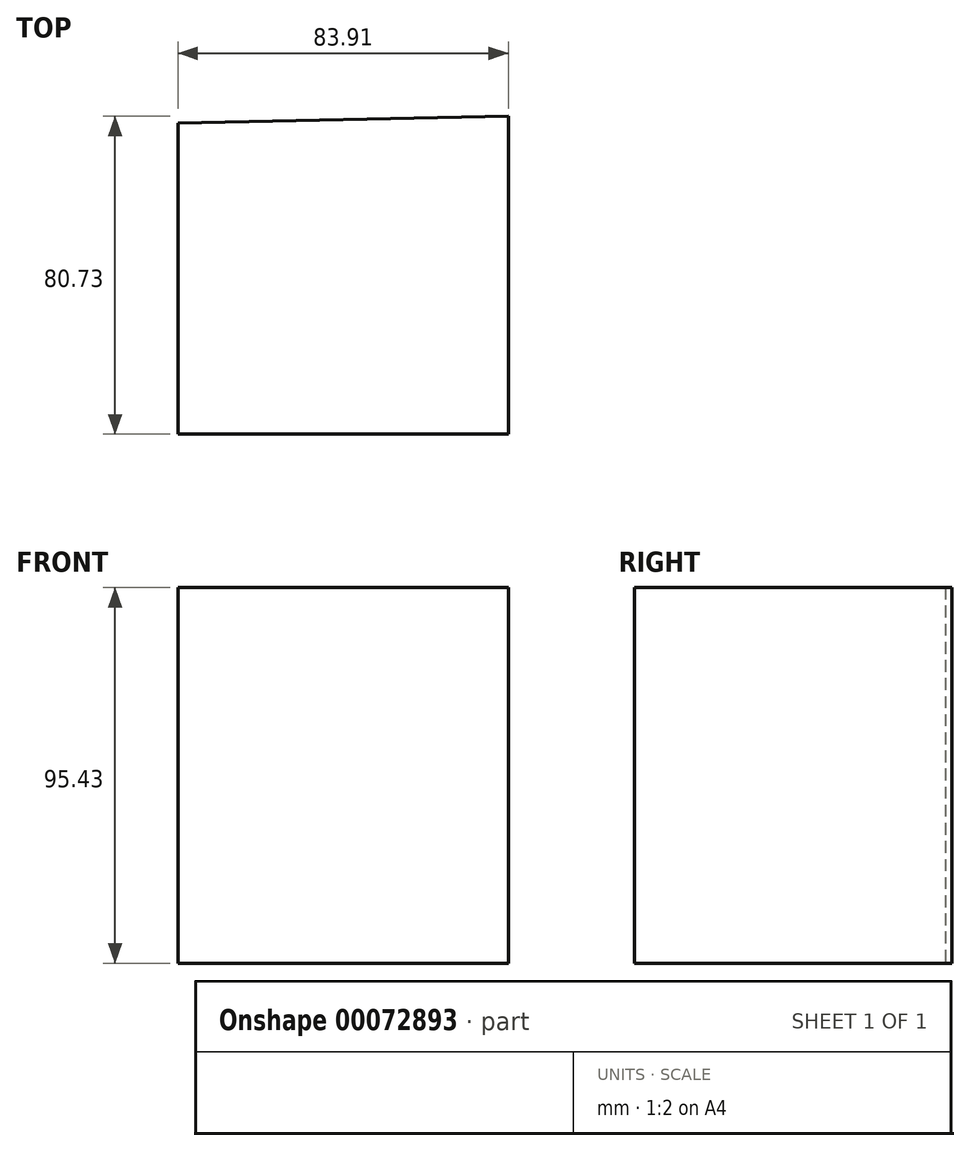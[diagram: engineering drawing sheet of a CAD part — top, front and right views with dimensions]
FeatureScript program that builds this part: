
annotation { "Feature Type Name" : "Feature", "Feature Type Description" : "" }
export const myFeature = defineFeature(function(context is Context, id is Id, definition is map)
    precondition{}
    {
        {
            var Q0;
            Q0=qCreatedBy(makeId("Top.planeOp"),FACE);
            var sketch = newSketch(context, id + "F0", { "sketchPlane" : qUnion([Q0])});
            skLineSegment(sketch, "E0", {"start": v(-43.98, 36.9) * mm, "end": v(-43.98, -42.1) * mm});
            skLineSegment(sketch, "E1", {"start": v(39.93, -42.1) * mm, "end": v(39.93, 38.63) * mm});
            skLineSegment(sketch, "E2", {"start": v(39.93, 38.63) * mm, "end": v(-43.98, 36.9) * mm});
            skLineSegment(sketch, "E3", {"start": v(-43.98, -42.1) * mm, "end": v(39.93, -42.1) * mm});
            skSolve(sketch);
        }
        {
            var Q0;
            Q0=makeQuery(id+"F0.imprint","IMPRINT",FACE,{"disambiguationData":[TD([[makeQuery(id+"F0.imprint","IMPRINT",EDGE,{"derivedFrom":sQuery(id+"F0.wireOp",EDGE,"E0")}),1.0]])]});
            extrude(context, id + "F1", {"entities" : qUnion([Q0]), "depth" : 95.43 * mm});
        }
    });
